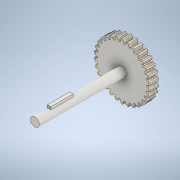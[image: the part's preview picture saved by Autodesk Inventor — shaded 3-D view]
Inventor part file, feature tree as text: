
AUTODESK INVENTOR PART (.ipt)
format: ipt  version: 2021 (Build 250183000, 183)  size: 327,168 bytes
history: native  units: mm (DEFAULTED — no unit token found)
features: sketch x7, extrude x5, plane x3, other x3
ambient origin geometry x8: Origin, YZ Plane, XZ Plane, XY Plane, X Axis, Y Axis, Z Axis, Center Point
bodies: Solid1 (feature_tree)
feature tree (18):
  extrude  "Extrusion1"  Depth=5.0mm TaperAngle=0.0deg
  plane  "Work Plane2"
  plane  "Work Plane8"
  plane  "Work Plane9"
  other  "Spur Gear"
  extrude  "Extrusion3"  Depth=10.0mm TaperAngle=0.0deg
  sketch  "Sketch6"  dims[d39=0.0mm d41=0.0mm]
  extrude  "Extrusion4"  Depth=1.047198mm TaperAngle=0.0deg
  extrude  "Extrusion5"  TaperAngle=0.0deg  [1 undecoded]
  extrude  "Extrusion6"  Depth=22.5mm
  sketch  "Sketch1"  dims[d0=31.6mm d1=5.0mm d2=0.0mm]
  sketch  "Sketch2"  dims[d3=30.0mm d4=10.0mm d5=0.0mm]
  other  "Srf1"
  sketch  "Sketch5"  dims[d16=22.5mm d17=0.0mm d34=1.047198mm]
  sketch  "Sketch7"  dims[d43=22.5mm d46=22.5mm]
  sketch  "Sketch8"  dims[d47=0.0mm d48=0.0mm]
  sketch  "Sketch9"  dims[d63=5.0mm d68=41.0mm d69=0.0mm d70=2.0mm d71=1.5mm d72=12.5mm d73=0.0mm d74=5.0mm d75=8.0mm d76=0.0mm d77=8.0mm d78=0.0mm d59=0.5mm d60=0.872665mm d61=0.5mm d62=0.872665mm d79=0.5mm d80=0.872665mm]
  other  "Pitch Diameter"
note: 1 required parameter value undecoded (feature->parameter linkage not recoverable at this tier; creation-order binding heuristic only, values carry confidence <= 0.55)
